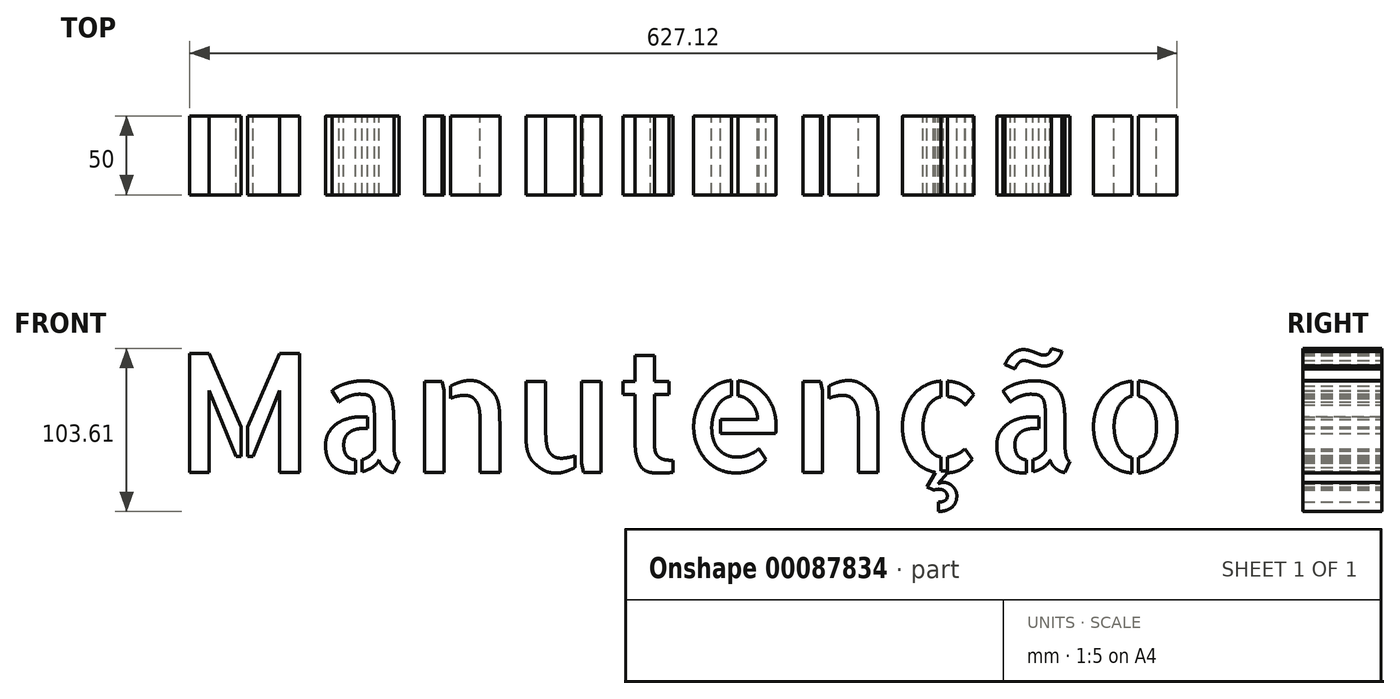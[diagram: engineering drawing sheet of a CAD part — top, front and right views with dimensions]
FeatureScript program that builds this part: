
annotation { "Feature Type Name" : "Feature", "Feature Type Description" : "" }
export const myFeature = defineFeature(function(context is Context, id is Id, definition is map)
    precondition{}
    {
        {
            var Q0;
            Q0=qCreatedBy(makeId("Front.planeOp"),FACE);
            var sketch = newSketch(context, id + "F0", { "sketchPlane" : qUnion([Q0])});
            skText(sketch, "E0", { "text": "Manutenção", "fontName": "AllertaStencil-Regular.ttf"});
            const initialGuessF0  = {"E0": [-0.15779, -0.03156, 1, 0, 0.0754]};
            skSetInitialGuess(sketch, initialGuessF0);
            skSolve(sketch);
        }
        {
            var Q0;
            Q0 = qSketchRegion(id + "F0", true);
            extrude(context, id + "F1", {"entities" : qUnion([Q0]), "endBound" : BoundingType.SYMMETRIC, "depth" : 50 * mm});
        }
    });
